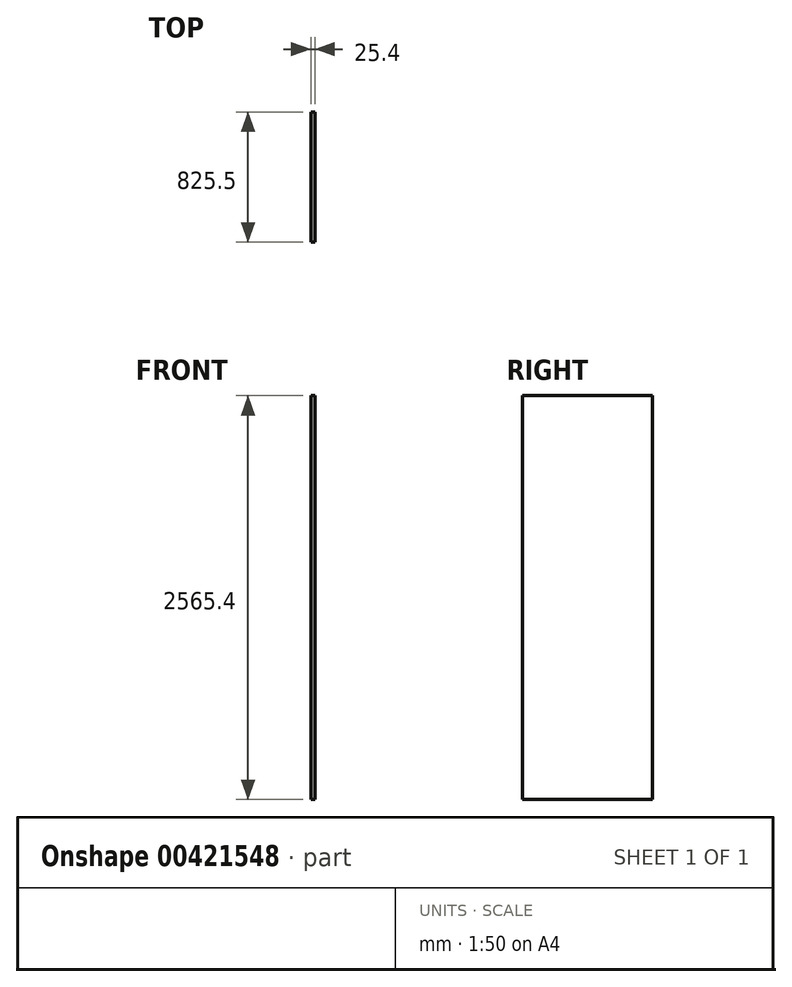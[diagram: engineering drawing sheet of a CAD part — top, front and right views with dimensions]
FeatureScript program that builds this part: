
annotation { "Feature Type Name" : "Feature", "Feature Type Description" : "" }
export const myFeature = defineFeature(function(context is Context, id is Id, definition is map)
    precondition{}
    {
        {
            var Q0;
            Q0=qCreatedBy(makeId("Right.planeOp"),FACE);
            var sketch = newSketch(context, id + "F0", { "sketchPlane" : qUnion([Q0])});
            skLineSegment(sketch, "E0.bottom", {"start": v(0, 0) * mm, "end": v(-825.5, 0) * mm});
            skLineSegment(sketch, "E0.top", {"start": v(0, 2565.4) * mm, "end": v(-825.5, 2565.4) * mm});
            skLineSegment(sketch, "E0.left", {"start": v(0, 0) * mm, "end": v(0, 2565.4) * mm});
            skLineSegment(sketch, "E0.right", {"start": v(-825.5, 0) * mm, "end": v(-825.5, 2565.4) * mm});
            skSolve(sketch);
        }
        {
            var Q0;
            Q0=makeQuery(id+"F0.imprint","IMPRINT",FACE,{"disambiguationData":[TD([[makeQuery(id+"F0.imprint","IMPRINT",EDGE,{"derivedFrom":sQuery(id+"F0.wireOp",EDGE,"E0.bottom")}),-1.0]])]});
            extrude(context, id + "F1", {"entities" : qUnion([Q0]), "depth" : 25.4 * mm});
        }
    });
